# Revit family: Toilet_Elongated-American_Standard-Aspirations-252AA89X_Series
name_source: partatom
category: Plumbing Fixtures
units: mm (PartAtom-declared; Revit-internal decimal feet)

## family parameters
Always vertical = No
Cut with Voids When Loaded = No
OmniClass Number = 23.45.05.21.11
OmniClass Title = Water Closets
Part Type = Normal
Room Calculation Point = No
Round Connector Dimension = Use Diameter
Shared = Yes
Work Plane-Based = Yes

## types (2) — shared parameters
5036A65G Elongated Luxury Seat included = Yes
ADA Compliant = Yes
ASME A112.18.1/CSA B125.1 = Yes
Assembly Code = D2010110
Bowl Shape = Elongated
CW Connection = Yes
CWFU = 5
Cold Water Connection Diameter = 1/2"
Cold Water Connection Height = 5 1/2"
Cold Water Connection Radius = 1/4"
Default Elevation = 0"
Description = Aspirations™ Skirted Two-Piece Chair Height Elongated Toilet with Seat VITREOUS CHINA
EPA WaterSense® Certified = Yes
Finish = Vitreous China-American Standard-020-White
Flush Rate = 4.8 Lpf/1.28 gpf
HW Connection = No
Height = 30 11/16"
Installation Type = Floor Mounted
Length = 30 3/16"
Lever Material = Metal-American Standard-Chrome
Manufacturer = American Standard
Material = Vitreous China-American Standard-020-White
Price = Prices may vary. Please consult Manufacturer Representative for most up-to-date price list.
SUPPLY POSITION 1 = Yes
SUPPLY POSITION 2 = No
Supply Location = 9"
Toilet Seat Material = Plastic-American Standard-020-White
Type Comments = Available Colors: White
URL = http://www.americanstandard.ca
Vent Connection = No
WFU = 5
Warranty Information = 10 year warranty on all mechanical parts, and 1 year warranty on seat
Waste Connection = Yes
Waste Connection Diameter = 3"
Waste Connection Radius = 1 1/2"
Width = 14 11/16"
zero-valued in all types: HWFU

## per-type parameters (varying)
| type | Left Hand Trip Lever | Right Hand Trip Lever |
| 252AA899.020 | Yes | No |
| 252AA898.020 | No | Yes |

note: column(s) folded — value = type name in every type: Model

## geometry (parser evidence)
native form markers: Sweep x2
no freeform markers — native parametric forms only
